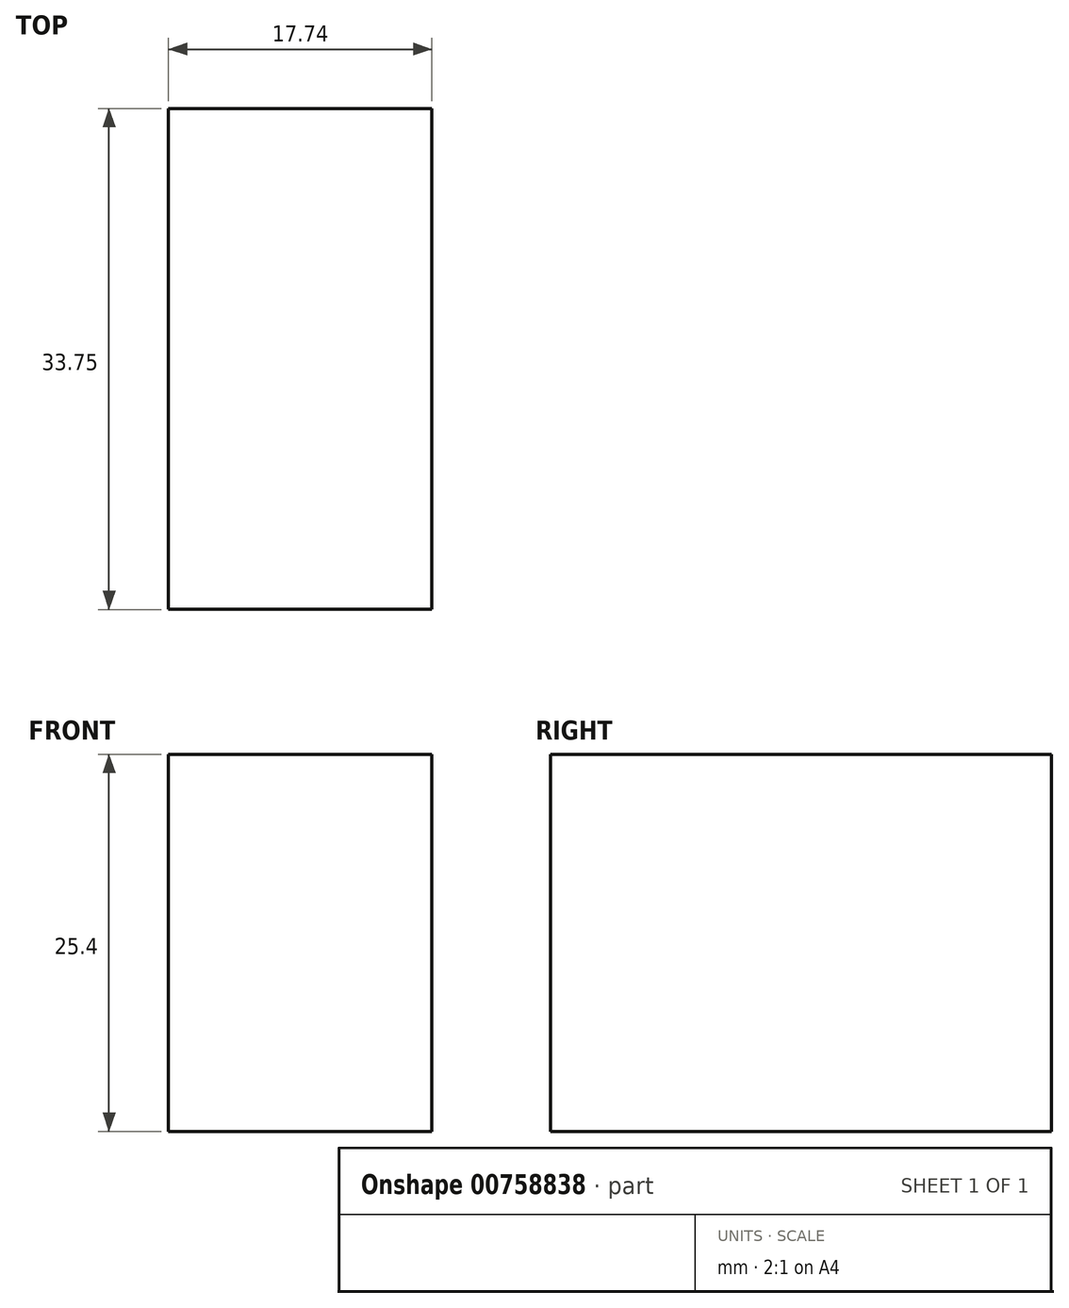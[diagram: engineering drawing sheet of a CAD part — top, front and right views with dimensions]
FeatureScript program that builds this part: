
annotation { "Feature Type Name" : "Feature", "Feature Type Description" : "" }
export const myFeature = defineFeature(function(context is Context, id is Id, definition is map)
    precondition{}
    {
        {
            var Q0;
            Q0=qCreatedBy(makeId("Top.planeOp"),FACE);
            var sketch = newSketch(context, id + "F0", { "sketchPlane" : qUnion([Q0])});
            skLineSegment(sketch, "E0.bottom", {"start": v(-47.18, 45.15) * mm, "end": v(-29.44, 45.15) * mm});
            skLineSegment(sketch, "E0.top", {"start": v(-47.18, 11.4) * mm, "end": v(-29.44, 11.4) * mm});
            skLineSegment(sketch, "E0.left", {"start": v(-47.18, 45.15) * mm, "end": v(-47.18, 11.4) * mm});
            skLineSegment(sketch, "E0.right", {"start": v(-29.44, 45.15) * mm, "end": v(-29.44, 11.4) * mm});
            skLineSegment(sketch, "E1.bottom", {"start": v(21.75, 44.24) * mm, "end": v(43.95, 44.24) * mm});
            skLineSegment(sketch, "E1.top", {"start": v(21.75, 9.2) * mm, "end": v(43.95, 9.2) * mm});
            skLineSegment(sketch, "E1.left", {"start": v(21.75, 44.24) * mm, "end": v(21.75, 9.2) * mm});
            skLineSegment(sketch, "E1.right", {"start": v(43.95, 44.24) * mm, "end": v(43.95, 9.2) * mm});
            skSolve(sketch);
        }
        {
            var Q0;
            Q0=makeQuery(id+"F0.imprint","IMPRINT",FACE,{"disambiguationData":[TD([[makeQuery(id+"F0.imprint","IMPRINT",EDGE,{"derivedFrom":sQuery(id+"F0.wireOp",EDGE,"E0.bottom")}),-1.0]])]});
            extrude(context, id + "F1", {"entities" : qUnion([Q0]), "depth" : 25.4 * mm, "offsetDistance" : 25.4 * mm});
        }
    });
